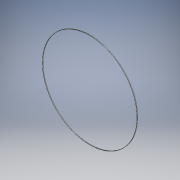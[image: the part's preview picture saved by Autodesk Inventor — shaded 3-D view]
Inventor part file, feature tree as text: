
AUTODESK INVENTOR PART (.ipt)
format: ipt  version: 2019 (Build 230136000, 136)  size: 104,960 bytes
history: native  units: mm
features: extrude x2, sketch x2
ambient origin geometry x8: Origin, YZ Plane, XZ Plane, XY Plane, X Axis, Y Axis, Z Axis, Center Point
bodies: Solid1 (feature_tree)
feature tree (4):
  extrude  "Extrusion1"  Depth=2.7mm TaperAngle=0.0deg
  extrude  "Extrusion2"  Depth=0.27mm TaperAngle=0.0deg
  sketch  "Sketch1"  dims[d0=415.34mm d1=2.7mm d2=0.0mm]
  sketch  "Sketch2"  dims[d3=414.0mm d4=0.27mm d5=0.0mm]
